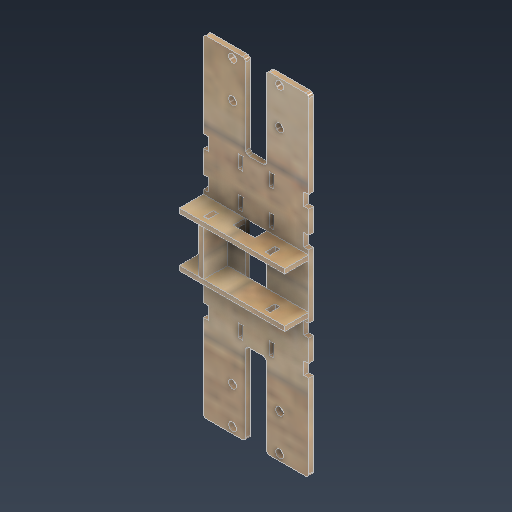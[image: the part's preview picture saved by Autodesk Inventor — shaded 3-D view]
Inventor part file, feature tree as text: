
AUTODESK INVENTOR PART (.ipt)
format: ipt  version: 2025.3 (Build 293356000, 356)  size: 516,096 bytes
history: native  units: mm
features: sketch x6, extrude x5, other x4
ambient origin geometry x8: Origin, YZ Plane, XZ Plane, XY Plane, X Axis, Y Axis, Z Axis, Center Point
bodies: Body1 (feature_tree), Body2 (feature_tree), Body3 (feature_tree), Body4 (feature_tree)
feature tree (15):
  other  "實體1"
  extrude  "擠出1"  Depth=66.0mm
  sketch  "草圖3"
  extrude  "擠出4"  Depth=208.0mm
  extrude  "擠出5"  Depth=5.0mm
  extrude  "擠出6"  Depth=4.0mm
  extrude  "擠出7"  Depth=23.0mm
  sketch  "草圖1"
  sketch  "草圖5"
  sketch  "草圖6"
  other  "實體2"
  sketch  "草圖7"
  sketch  "草圖8"
  other  "實體3"
  other  "實體4"
